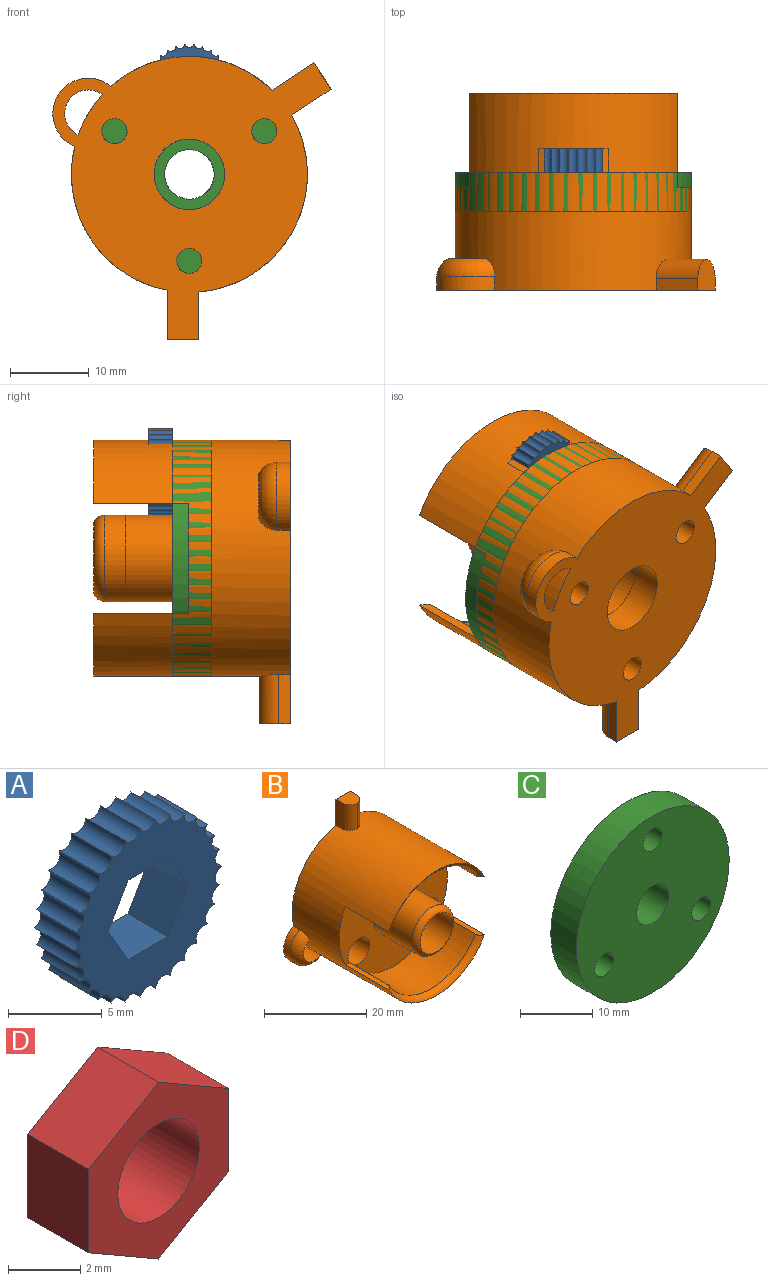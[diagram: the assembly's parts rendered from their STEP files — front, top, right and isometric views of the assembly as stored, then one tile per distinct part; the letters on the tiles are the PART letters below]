
ASSEMBLY  parts=4 mates=3
PART A: 38 faces, bbox 11.1x3x11 mm
  f0: plane 3x2.6mm, normal (0.87,0,-0.5), area 9mm2, adj f1,f35,f36,f37
  f1: plane 3x3mm, normal (0,0,-1), area 9mm2, adj f0,f2,f36,f37
  f2: plane 3x2.6mm, normal (-0.87,0,-0.5), area 9mm2, adj f1,f3,f36,f37
  f3: plane 3x2.6mm, normal (-0.87,0,0.5), area 9mm2, adj f2,f4,f36,f37
  f4: plane 3x3mm, normal (0,0,1), area 9mm2, adj f3,f35,f36,f37
  f5: cylinder r=0.62mm len=3mm, axis (0,1,0), area 4.5mm2, adj f6,f34,f36,f37
  f6: cylinder r=0.62mm len=3mm, axis (0,1,0), area 4.5mm2, adj f5,f7,f36,f37
  f7: cylinder r=0.62mm len=3mm, axis (0,1,0), area 4.5mm2, adj f6,f8,f36,f37
  f8: cylinder r=0.62mm len=3mm, axis (0,1,0), area 4.5mm2, adj f7,f9,f36,f37
  f9: cylinder r=0.62mm len=3mm, axis (0,1,0), area 4.5mm2, adj f8,f10,f36,f37
  f10: cylinder r=0.62mm len=3mm, axis (0,1,0), area 4.5mm2, adj f9,f11,f36,f37
  f11: cylinder r=0.62mm len=3mm, axis (0,1,0), area 4.5mm2, adj f10,f12,f36,f37
  f12: cylinder r=0.62mm len=3mm, axis (0,1,0), area 4.5mm2, adj f11,f13,f36,f37
  f13: cylinder r=0.62mm len=3mm, axis (0,1,0), area 4.5mm2, adj f12,f14,f36,f37
  f14: cylinder r=0.62mm len=3mm, axis (0,1,0), area 4.5mm2, adj f13,f15,f36,f37
  f15: cylinder r=0.62mm len=3mm, axis (0,1,0), area 4.5mm2, adj f14,f16,f36,f37
  f16: cylinder r=0.62mm len=3mm, axis (0,1,0), area 4.5mm2, adj f15,f17,f36,f37
  f17: cylinder r=0.62mm len=3mm, axis (0,1,0), area 4.5mm2, adj f16,f18,f36,f37
  f18: cylinder r=0.62mm len=3mm, axis (0,1,0), area 4.5mm2, adj f17,f19,f36,f37
  f19: cylinder r=0.62mm len=3mm, axis (0,1,0), area 4.5mm2, adj f18,f20,f36,f37
  f20: cylinder r=0.62mm len=3mm, axis (0,1,0), area 4.5mm2, adj f19,f21,f36,f37
  f21: cylinder r=0.62mm len=3mm, axis (0,1,0), area 4.5mm2, adj f20,f22,f36,f37
  f22: cylinder r=0.62mm len=3mm, axis (0,1,0), area 4.5mm2, adj f21,f23,f36,f37
  f23: cylinder r=0.62mm len=3mm, axis (0,1,0), area 4.5mm2, adj f22,f24,f36,f37
  f24: cylinder r=0.62mm len=3mm, axis (0,1,0), area 4.5mm2, adj f23,f25,f36,f37
  f25: cylinder r=0.62mm len=3mm, axis (0,1,0), area 4.5mm2, adj f24,f26,f36,f37
  f26: cylinder r=0.62mm len=3mm, axis (0,1,0), area 4.5mm2, adj f25,f27,f36,f37
  f27: cylinder r=0.62mm len=3mm, axis (0,1,0), area 4.5mm2, adj f26,f28,f36,f37
  f28: cylinder r=0.62mm len=3mm, axis (0,1,0), area 4.5mm2, adj f27,f29,f36,f37
  f29: cylinder r=0.62mm len=3mm, axis (0,1,0), area 4.5mm2, adj f28,f30,f36,f37
  f30: cylinder r=0.62mm len=3mm, axis (0,1,0), area 4.5mm2, adj f29,f31,f36,f37
  f31: cylinder r=0.62mm len=3mm, axis (0,1,0), area 4.5mm2, adj f30,f32,f36,f37
  f32: cylinder r=0.62mm len=3mm, axis (0,1,0), area 4.5mm2, adj f31,f33,f36,f37
  f33: cylinder r=0.62mm len=3mm, axis (0,1,0), area 4.5mm2, adj f32,f34,f36,f37
  f34: cylinder r=0.62mm len=3mm, axis (0,1,0), area 4.5mm2, adj f5,f33,f36,f37
  f35: plane 3x2.6mm, normal (0.87,0,0.5), area 9mm2, adj f0,f4,f36,f37
  f36: plane 11.09x11.03mm, normal (0,-1,0), area 62.7mm2, adj f0,f1,f2,f3,f4,f5,f6,f7
  f37: plane 11.09x11.03mm, normal (0,1,0), area 62.7mm2, adj f0,f1,f2,f3,f4,f5,f6,f7
PART B: 41 faces, bbox 35.6x25.3x38 mm
  f0: cylinder r=1.6mm len=3.2mm, axis (0,1,0), area 10.1mm2, adj f20,f27
  f1: cylinder r=1.6mm len=3.2mm, axis (0,1,0), area 10.1mm2, adj f18,f23
  f2: cylinder r=1.6mm len=3.2mm, axis (0,1,0), area 10.1mm2, adj f16,f26
  f3: cylinder r=15mm len=30mm, axis (0,1,0), area 1976.1mm2, adj f8,f9,f10,f11,f12,f13,f15,f22
  f4: cylinder r=14mm len=24.25mm, axis (0,-1,0), area 310.4mm2, adj f8,f10,f12,f15
  f5: cylinder r=4.5mm len=21mm, axis (0,1,0), area 593.8mm2, adj f14,f34
  f6: cylinder r=5.5mm len=11mm, axis (0,-1,0), area 365.8mm2, adj f8,f14
  f7: cylinder r=14mm len=24.25mm, axis (0,-1,0), area 310.4mm2, adj f8,f9,f11,f13
  f8: plane 30x28mm, normal (0,-1,0), area 465.1mm2, adj f3,f4,f6,f7,f9,f10,f11,f12
  f9: plane 12.22x1.36mm, normal (0,0,1), area 13.3mm2, adj f3,f7,f8,f13
  f10: plane 12.22x1.36mm, normal (0,0,-1), area 13.3mm2, adj f3,f4,f8,f15
  f11: plane 12.22x1.36mm, normal (0,0,1), area 13.3mm2, adj f3,f7,f8,f13
  f12: plane 12.22x1.36mm, normal (0,0,-1), area 13.3mm2, adj f3,f4,f8,f15
  f13: torus R=15.5mm, axis (0,-1,0), area 56.5mm2, adj f3,f7,f9,f11
  f14: torus R=4mm, axis (0,-1,0), area 59.7mm2, adj f5,f6
  f15: torus R=15.5mm, axis (0,-1,0), area 56.5mm2, adj f3,f4,f10,f12
  f16: plane 6x6mm, normal (0,-1,0), area 20.2mm2, adj f2,f17
  f17: cylinder r=3mm len=8mm, axis (0,-1,0), area 150.8mm2, adj f8,f16
  f18: plane 6x6mm, normal (0,-1,0), area 20.2mm2, adj f1,f19
  f19: cylinder r=3mm len=8mm, axis (0,-1,0), area 150.8mm2, adj f8,f18
  f20: plane 6x6mm, normal (0,-1,0), area 20.2mm2, adj f0,f21
  f21: cylinder r=3mm len=8mm, axis (0,-1,0), area 150.8mm2, adj f8,f20
  f22: plane 36x35.37mm, normal (0,1,0), area 687.2mm2, adj f3,f23,f24,f25,f26,f27,f28,f29
  f23: cylinder r=1.6mm len=4mm, axis (0,-1,0), area 40.3mm2, adj f1,f22
  f24: plane 3.95x3.35mm, normal (0.84,0,-0.55), area 13.3mm2, adj f22,f28,f33,f38,f39
  f25: cylinder r=3mm len=5.71mm, axis (0,-1,0), area 40.1mm2, adj f3,f22,f35
  f26: cylinder r=1.6mm len=4mm, axis (0,-1,0), area 40.1mm2, adj f2,f22
  f27: cylinder r=1.6mm len=4mm, axis (0,-1,0), area 40.3mm2, adj f0,f22
  f28: plane 5.04x3.3mm, normal (0.55,0,0.84), area 9mm2, adj f3,f22,f24,f38
  f29: plane 6.05x1.5mm, normal (1,0,0), area 9.1mm2, adj f3,f22,f30,f36
  f30: plane 4x3.95mm, normal (0,0,1), area 13.3mm2, adj f22,f29,f31,f36,f37
  f31: plane 6.27x1.5mm, normal (-1,0,0), area 9.4mm2, adj f3,f22,f30,f37
  f32: cylinder r=4.5mm len=8.66mm, axis (0,-1,0), area 26.5mm2, adj f3,f22,f35
  f33: plane 5.31x3.47mm, normal (-0.55,0,-0.84), area 9.5mm2, adj f3,f22,f24,f39
  f34: plane 9x9mm, normal (0,-1,0), area 0.4mm2, adj f5,f40
  f35: torus R=2mm, axis (0,-1,0), area 39.1mm2, adj f3,f25,f32
  f36: cylinder r=2.5mm len=6.05mm, axis (0,0,-1), area 20.7mm2, adj f3,f29,f30,f37
  f37: cylinder r=2.5mm len=6.27mm, axis (0,0,1), area 21mm2, adj f3,f30,f31,f36
  f38: cylinder r=2.5mm len=6.15mm, axis (0.84,0,-0.55), area 20.7mm2, adj f3,f24,f28,f39
  f39: cylinder r=2.5mm len=6.4mm, axis (-0.84,0,0.55), area 21.2mm2, adj f3,f24,f33,f38
  f40: cylinder r=4.49mm len=8.97mm, axis (0,-1,0), area 112.8mm2, adj f22,f34
PART C: 9 faces, bbox 30x11x30 mm
  f0: cylinder r=15mm len=30mm, axis (0,1,0), area 471.2mm2, adj f1,f2
  f1: plane 30x30mm, normal (0,-1,0), area 643.4mm2, adj f0,f3,f6,f7,f8
  f2: plane 30x30mm, normal (0,1,0), area 579.6mm2, adj f0,f4,f6,f7,f8
  f3: cylinder r=3.15mm len=11mm, axis (0,-1,0), area 217.7mm2, adj f1,f5
  f4: cylinder r=5.5mm len=11mm, axis (0,-1,0), area 207.3mm2, adj f2,f5
  f5: plane 11x11mm, normal (0,1,0), area 63.9mm2, adj f3,f4
  f6: cylinder r=1.85mm len=5mm, axis (0,-1,0), area 58.1mm2, adj f1,f2
  f7: cylinder r=1.85mm len=5mm, axis (0,-1,0), area 58.1mm2, adj f1,f2
  f8: cylinder r=1.85mm len=5mm, axis (0,-1,0), area 58.1mm2, adj f1,f2
PART D: 9 faces, bbox 5.5x2.4x6 mm
  f0: plane 2.75x2.4mm, normal (0.5,0,0.87), area 7.6mm2, adj f1,f6,f7,f8
  f1: plane 2.75x2.4mm, normal (-0.5,0,0.87), area 7.6mm2, adj f0,f2,f7,f8
  f2: plane 2.84x2.4mm, normal (-1,0,0), area 6.8mm2, adj f1,f3,f7,f8
  f3: plane 2.75x2.4mm, normal (-0.5,0,-0.87), area 7.6mm2, adj f2,f4,f7,f8
  f4: plane 2.75x2.4mm, normal (0.5,0,-0.87), area 7.6mm2, adj f3,f6,f7,f8
  f5: cylinder r=1.6mm len=3.2mm, axis (0,1,0), area 24.1mm2, adj f7,f8
  f6: plane 2.84x2.4mm, normal (1,0,0), area 6.8mm2, adj f0,f4,f7,f8
  f7: plane 6.01x5.5mm, normal (0,-1,0), area 16.3mm2, adj f0,f1,f2,f3,f4,f5,f6
  f8: plane 6.01x5.5mm, normal (0,1,0), area 16.3mm2, adj f0,f1,f2,f3,f4,f5,f6
PLACE A rot(axis=(1,0,0),180deg) t=(-39.88,5.21,43.64)mm
PLACE B rot(axis=(1,0,0),180deg) t=(11.83,-5.76,-7.92)mm
PLACE C t=(-40.46,5.21,-7.92)mm
PLACE D rot(axis=(0,1,0),90deg) t=(11.83,7.61,3.08)mm
MATE slider A.f37 <-> C.f8  axis (0,-1,0) through (11.83,5.21,3.08)mm
MATE slider B.f5 <-> C.f0  axis (0,1,0) through (11.83,-5.76,-7.92)mm
MATE fastened D.f5 <-> C.f8  axis (0,1,0) through (11.83,5.21,3.08)mm
